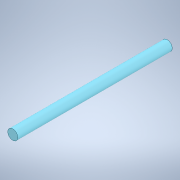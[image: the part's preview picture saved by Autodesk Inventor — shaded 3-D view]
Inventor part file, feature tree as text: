
AUTODESK INVENTOR PART (.ipt)
format: ipt  version: 2022 (Build 260153000, 153)  size: 101,888 bytes
history: native  units: in
note: dims shown in document units (in); Inventor stores cm internally (conversion verified against a paired STEP export)
features: extrude x1, sketch x1
ambient origin geometry x8: Origin, YZ Plane, XZ Plane, XY Plane, X Axis, Y Axis, Z Axis, Center Point
bodies: Solid1 (feature_tree)
feature tree (2):
  extrude  "Extrusion1"  Depth=3.937in
  sketch  "Sketch2"  dims[d0=3.937in d1=0.0in d2=0.2559in]
